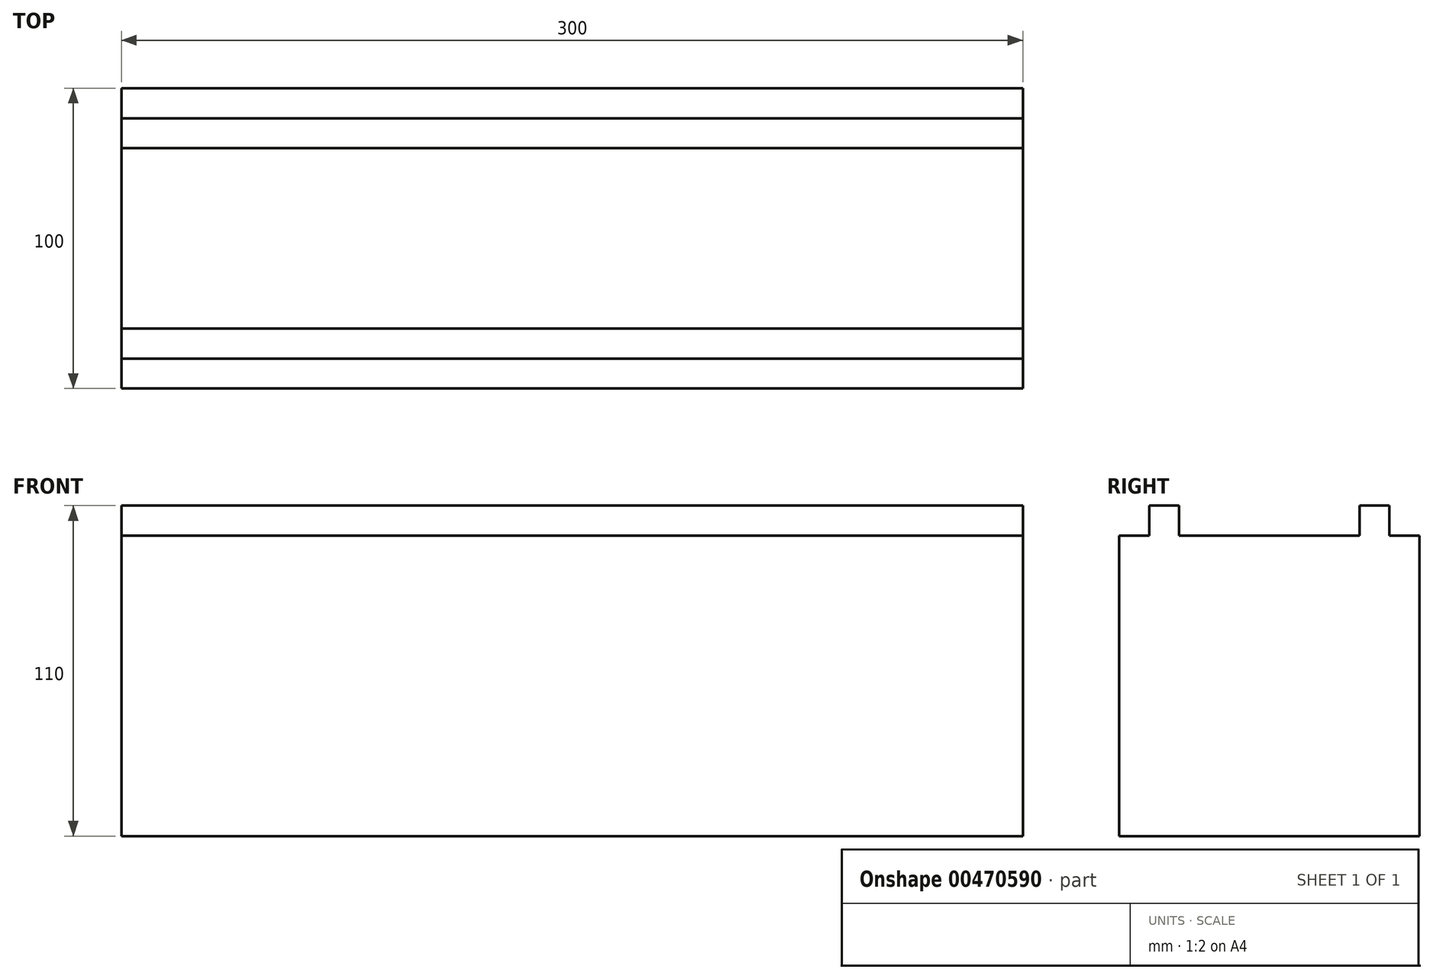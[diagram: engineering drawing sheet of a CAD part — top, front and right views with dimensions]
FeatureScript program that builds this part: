
annotation { "Feature Type Name" : "Feature", "Feature Type Description" : "" }
export const myFeature = defineFeature(function(context is Context, id is Id, definition is map)
    precondition{}
    {
        {
            var Q0;
            Q0=qCreatedBy(makeId("Top.planeOp"),FACE);
            var sketch = newSketch(context, id + "F0", { "sketchPlane" : qUnion([Q0])});
            skLineSegment(sketch, "E0.bottom", {"start": v(150, 50) * mm, "end": v(-150, 50) * mm});
            skLineSegment(sketch, "E0.top", {"start": v(150, -50) * mm, "end": v(-150, -50) * mm});
            skLineSegment(sketch, "E0.left", {"start": v(150, 50) * mm, "end": v(150, -50) * mm});
            skLineSegment(sketch, "E0.right", {"start": v(-150, 50) * mm, "end": v(-150, -50) * mm});
            skPoint(sketch, "E0.middle", {"position": v(0, 0) * mm});
            skSolve(sketch);
        }
        {
            var Q0;
            Q0=makeQuery(id+"F0.imprint","IMPRINT",FACE,{"disambiguationData":[TD([[makeQuery(id+"F0.imprint","IMPRINT",EDGE,{"derivedFrom":sQuery(id+"F0.wireOp",EDGE,"E0.bottom")}),1.0]])]});
            extrude(context, id + "F1", {"entities" : qUnion([Q0]), "endBound" : BoundingType.SYMMETRIC, "depth" : 100 * mm, "offsetDistance" : 25.4 * mm});
        }
        {
            var Q0;
            Q0=makeQuery(id+"F1.opExtrude","SWEPT_FACE",FACE,{"disambiguationData":[OSD([sQuery(id+"F0.wireOp",EDGE,"E0.right")])]});
            var sketch = newSketch(context, id + "F2", { "sketchPlane" : qUnion([Q0])});
            skLineSegment(sketch, "E1.bottom", {"start": v(-50, -50) * mm, "end": v(50, -50) * mm});
            skLineSegment(sketch, "E1.top", {"start": v(-50, 150) * mm, "end": v(50, 150) * mm});
            skLineSegment(sketch, "E1.left", {"start": v(-50, -50) * mm, "end": v(-50, 150) * mm});
            skLineSegment(sketch, "E1.right", {"start": v(50, -50) * mm, "end": v(50, 150) * mm});
            skSolve(sketch);
        }
        {
            var Q0;
            {var subQ0=sQuery(id+"F2.wireOp",EDGE,"E1.top");Q0=makeQuery(id+"F2.imprint","IMPRINT",FACE,{"disambiguationData":[TD([[makeQuery(id+"F2.imprint","IMPRINT",EDGE,{"derivedFrom":subQ0}),-1.0]])]});}
            var sketch = newSketch(context, id + "F3", { "sketchPlane" : qUnion([Q0])});
            skLineSegment(sketch, "E2.bottom", {"start": v(40, 50) * mm, "end": v(30, 50) * mm});
            skLineSegment(sketch, "E2.top", {"start": v(40, 60) * mm, "end": v(30, 60) * mm});
            skLineSegment(sketch, "E2.left", {"start": v(40, 50) * mm, "end": v(40, 60) * mm});
            skLineSegment(sketch, "E2.right", {"start": v(30, 50) * mm, "end": v(30, 60) * mm});
            skLineSegment(sketch, "E3.bottom", {"start": v(-40, 50) * mm, "end": v(-30, 50) * mm});
            skLineSegment(sketch, "E3.top", {"start": v(-40, 60) * mm, "end": v(-30, 60) * mm});
            skLineSegment(sketch, "E3.left", {"start": v(-40, 50) * mm, "end": v(-40, 60) * mm});
            skLineSegment(sketch, "E3.right", {"start": v(-30, 50) * mm, "end": v(-30, 60) * mm});
            skSolve(sketch);
        }
        {
            var Q0;
            Q0=makeQuery(id+"F3.imprint","IMPRINT",FACE,{"disambiguationData":[TD([[makeQuery(id+"F3.imprint","IMPRINT",EDGE,{"derivedFrom":sQuery(id+"F3.wireOp",EDGE,"E2.bottom")}),1.0]])]});
            var Q1;
            Q1=makeQuery(id+"F3.imprint","IMPRINT",FACE,{"disambiguationData":[TD([[makeQuery(id+"F3.imprint","IMPRINT",EDGE,{"derivedFrom":sQuery(id+"F3.wireOp",EDGE,"E3.bottom")}),1.0]])]});
            extrude(context, id + "F4", {"entities" : qUnion([Q0, Q1]), "operationType" : NewBodyOperationType.ADD, "oppositeDirection" : true, "depth" : 300 * mm, "offsetDistance" : 25.4 * mm});
        }
    });
